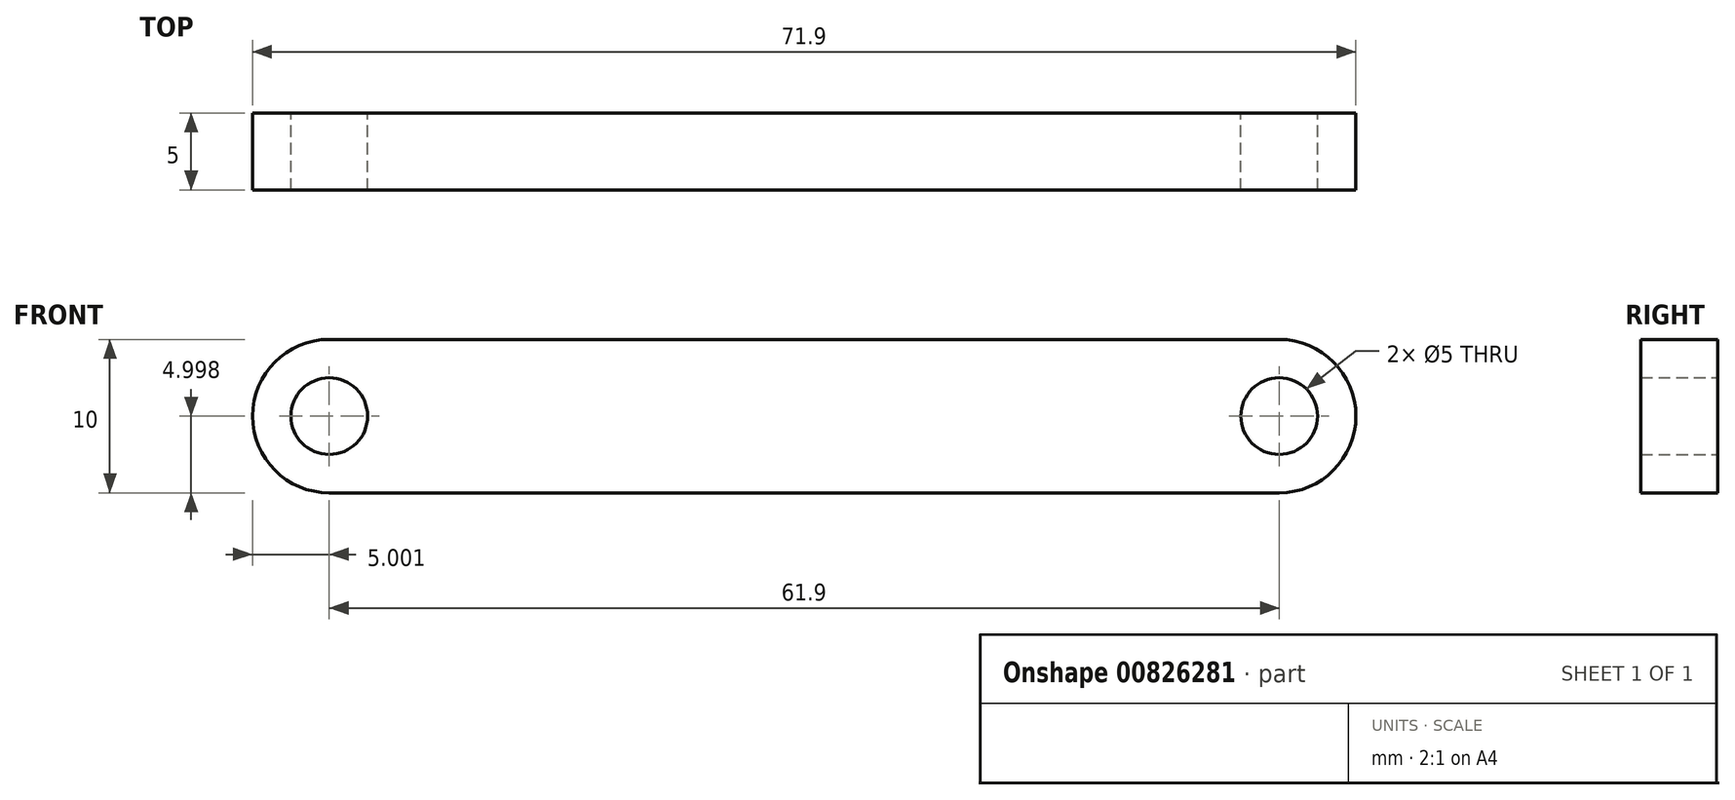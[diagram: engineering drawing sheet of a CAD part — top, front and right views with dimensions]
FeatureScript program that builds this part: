
annotation { "Feature Type Name" : "Feature", "Feature Type Description" : "" }
export const myFeature = defineFeature(function(context is Context, id is Id, definition is map)
    precondition{}
    {
        {
            var Q0;
            Q0=qCreatedBy(makeId("Front.planeOp"),FACE);
            var sketch = newSketch(context, id + "F0", { "sketchPlane" : qUnion([Q0])});
            skArc(sketch, "E0", {"start": v(-5.89, 19.29) * mm, "mid": v(-10.89, 14.29) * mm, "end": v(-5.89, 9.29) * mm});
            skArc(sketch, "E1", {"start": v(56.01, 9.29) * mm, "mid": v(61.01, 14.29) * mm, "end": v(56.01, 19.29) * mm});
            skLineSegment(sketch, "E2", {"start": v(-5.89, 19.29) * mm, "end": v(56.01, 19.29) * mm});
            skLineSegment(sketch, "E3", {"start": v(-5.89, 9.29) * mm, "end": v(56.01, 9.29) * mm});
            skCircle(sketch, "E4", {"center": v(-5.89, 14.29) * mm, "radius": 2.5 * mm});
            skCircle(sketch, "E5", {"center": v(56.01, 14.29) * mm, "radius": 2.5 * mm});
            skSolve(sketch);
        }
        {
            var Q0;
            Q0 = qSketchRegion(id + "F0", true);
            extrude(context, id + "F1", {"entities" : qUnion([Q0]), "depth" : 5 * mm, "offsetDistance" : 25 * mm});
        }
    });
